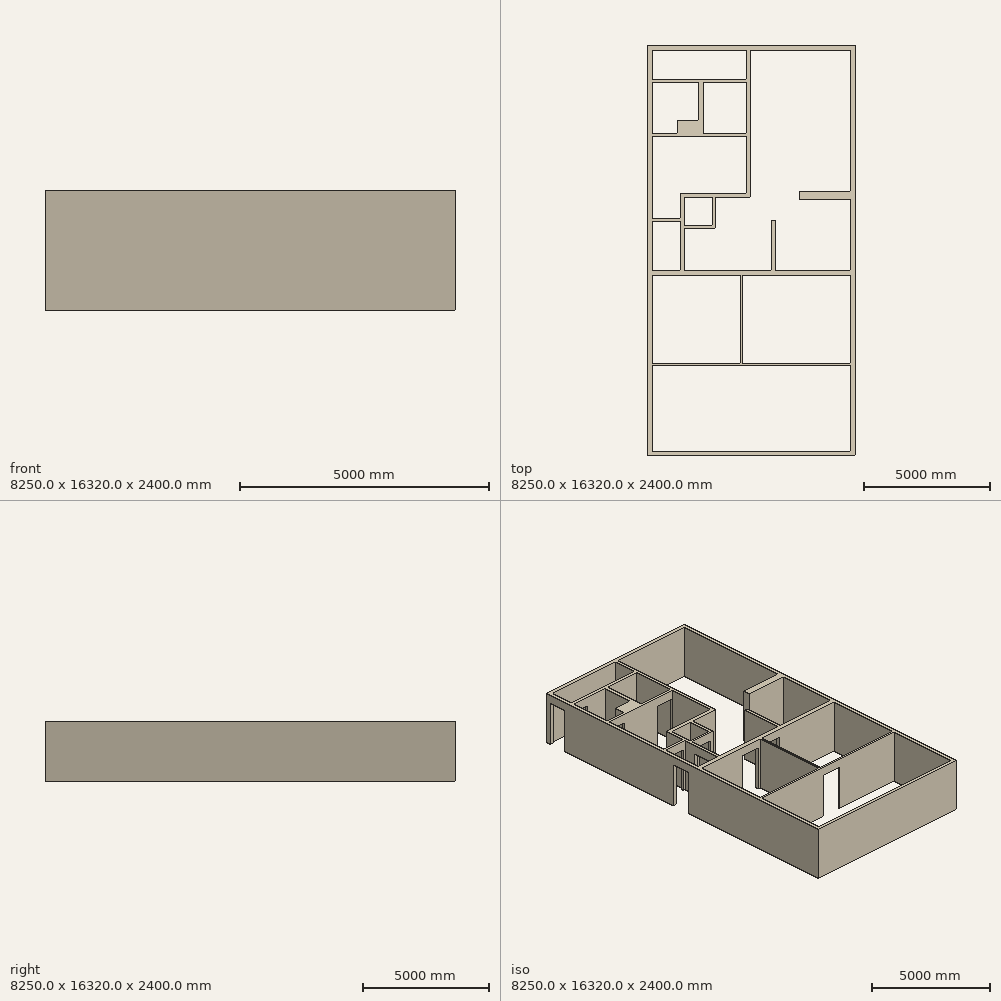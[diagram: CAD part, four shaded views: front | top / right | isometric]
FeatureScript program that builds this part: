
annotation { "Feature Type Name" : "Feature", "Feature Type Description" : "" }
export const myFeature = defineFeature(function(context is Context, id is Id, definition is map)
    precondition{}
    {
        {
            var Q0;
            Q0=qCreatedBy(makeId("Top.planeOp"),FACE);
            var sketch = newSketch(context, id + "F0", { "sketchPlane" : qUnion([Q0])});
            skLineSegment(sketch, "E0.bottom", {"start": v(-4125, 0) * mm, "end": v(4125, 0) * mm});
            skLineSegment(sketch, "E0.left", {"start": v(-4125, 0) * mm, "end": v(-4125, -9150) * mm});
            skLineSegment(sketch, "E0.right", {"start": v(4125, 0) * mm, "end": v(4125, -9150) * mm});
            skLineSegment(sketch, "E1.bottom", {"start": v(-3955, -200) * mm, "end": v(-195, -200) * mm});
            skLineSegment(sketch, "E1.top", {"start": v(-3955, -1340) * mm, "end": v(-195, -1340) * mm});
            skLineSegment(sketch, "E1.left", {"start": v(-3955, -200) * mm, "end": v(-3955, -1340) * mm});
            skLineSegment(sketch, "E1.right", {"start": v(-195, -200) * mm, "end": v(-195, -1340) * mm});
            skLineSegment(sketch, "E2.bottom", {"start": v(-3955, -1490) * mm, "end": v(-2105, -1490) * mm});
            skLineSegment(sketch, "E2.top", {"start": v(-3955, -3500) * mm, "end": v(-2105, -3500) * mm});
            skLineSegment(sketch, "E2.left", {"start": v(-3955, -1490) * mm, "end": v(-3955, -3500) * mm});
            skLineSegment(sketch, "E2.right", {"start": v(-2105, -1490) * mm, "end": v(-2105, -3500) * mm});
            skLineSegment(sketch, "E3.bottom", {"start": v(-1905, -1490) * mm, "end": v(-195, -1490) * mm});
            skLineSegment(sketch, "E3.top", {"start": v(-1905, -3500) * mm, "end": v(-195, -3500) * mm});
            skLineSegment(sketch, "E3.left", {"start": v(-1905, -1490) * mm, "end": v(-1905, -3500) * mm});
            skLineSegment(sketch, "E4.bottom", {"start": v(-3955, -3615) * mm, "end": v(-195, -3615) * mm});
            skLineSegment(sketch, "E4.top", {"start": v(-2825, -5885) * mm, "end": v(-195, -5885) * mm});
            skLineSegment(sketch, "E4.left", {"start": v(-3955, -3615) * mm, "end": v(-3955, -5885) * mm});
            skLineSegment(sketch, "E4.right", {"start": v(-195, -3615) * mm, "end": v(-195, -5885) * mm});
            skLineSegment(sketch, "E5.bottom", {"start": v(-2825, -6885) * mm, "end": v(-3955, -6885) * mm});
            skLineSegment(sketch, "E5.left", {"start": v(-2825, -6885) * mm, "end": v(-2825, -5885) * mm});
            skLineSegment(sketch, "E5.right", {"start": v(-3955, -6885) * mm, "end": v(-3955, -5885) * mm});
            skLineSegment(sketch, "E6.bottom", {"start": v(-3955, -8950) * mm, "end": v(-2825, -8950) * mm});
            skLineSegment(sketch, "E6.top", {"start": v(-3955, -7000) * mm, "end": v(-2825, -7000) * mm});
            skLineSegment(sketch, "E6.left", {"start": v(-3955, -8950) * mm, "end": v(-3955, -7000) * mm});
            skLineSegment(sketch, "E6.right", {"start": v(-2825, -8950) * mm, "end": v(-2825, -7000) * mm});
            skLineSegment(sketch, "E7.bottom", {"start": v(-2665, -6070) * mm, "end": v(-1545, -6070) * mm});
            skLineSegment(sketch, "E7.top", {"start": v(-2665, -7170) * mm, "end": v(-1545, -7170) * mm});
            skLineSegment(sketch, "E7.left", {"start": v(-2665, -6070) * mm, "end": v(-2665, -7170) * mm});
            skLineSegment(sketch, "E7.right", {"start": v(-1545, -6070) * mm, "end": v(-1545, -7170) * mm});
            skLineSegment(sketch, "E8.bottom", {"start": v(-45, -200) * mm, "end": v(3955, -200) * mm});
            skLineSegment(sketch, "E8.top", {"start": v(1905, -5800) * mm, "end": v(3955, -5800) * mm});
            skLineSegment(sketch, "E8.right", {"start": v(3955, -200) * mm, "end": v(3955, -5800) * mm});
            skLineSegment(sketch, "E9.bottom", {"start": v(3955, -8950) * mm, "end": v(955, -8950) * mm});
            skLineSegment(sketch, "E9.top", {"start": v(3955, -6120) * mm, "end": v(1905, -6120) * mm});
            skLineSegment(sketch, "E9.left", {"start": v(3955, -8950) * mm, "end": v(3955, -6120) * mm});
            skLineSegment(sketch, "E9.right", {"start": v(955, -8950) * mm, "end": v(955, -6950) * mm});
            skLineSegment(sketch, "E10.bottom", {"start": v(805, -8950) * mm, "end": v(-2665, -8950) * mm});
            skLineSegment(sketch, "E10.top", {"start": v(-1415, -7270) * mm, "end": v(-2665, -7270) * mm});
            skLineSegment(sketch, "E10.right", {"start": v(-2665, -8950) * mm, "end": v(-2665, -7270) * mm});
            skLineSegment(sketch, "E11.left", {"start": v(-1415, -6070) * mm, "end": v(-1415, -7270) * mm});
            skLineSegment(sketch, "E12", {"start": v(-2955, -3500) * mm, "end": v(-2955, -2970) * mm});
            skLineSegment(sketch, "E13", {"start": v(-2955, -2970) * mm, "end": v(-2105, -2970) * mm});
            skLineSegment(sketch, "E14", {"start": v(-195, -1490) * mm, "end": v(-195, -3500) * mm});
            skLineSegment(sketch, "E15", {"start": v(805, -8950) * mm, "end": v(805, -6950) * mm});
            skLineSegment(sketch, "E16", {"start": v(805, -6950) * mm, "end": v(955, -6950) * mm});
            skLineSegment(sketch, "E17", {"start": v(1905, -6120) * mm, "end": v(1905, -5800) * mm});
            skLineSegment(sketch, "E18", {"start": v(-1415, -6070) * mm, "end": v(-45, -6070) * mm});
            skLineSegment(sketch, "E19", {"start": v(-45, -6070) * mm, "end": v(-45, -200) * mm});
            skLineSegment(sketch, "E20", {"start": v(-4125, -9150) * mm, "end": v(4125, -9150) * mm});
            skLineSegment(sketch, "E21", {"start": v(-4125, -9150) * mm, "end": v(-4125, -16320) * mm});
            skLineSegment(sketch, "E22", {"start": v(-4125, -16320) * mm, "end": v(4125, -16320) * mm});
            skLineSegment(sketch, "E23", {"start": v(4125, -16320) * mm, "end": v(4125, -9150) * mm});
            skLineSegment(sketch, "E24", {"start": v(-3955, -9150) * mm, "end": v(-3955, -16150) * mm});
            skLineSegment(sketch, "E25", {"start": v(-3955, -16150) * mm, "end": v(3955, -16150) * mm});
            skLineSegment(sketch, "E26", {"start": v(3955, -16150) * mm, "end": v(3955, -9150) * mm});
            skLineSegment(sketch, "E27", {"start": v(-455, -9150) * mm, "end": v(-455, -12650) * mm});
            skLineSegment(sketch, "E28", {"start": v(-355, -12650) * mm, "end": v(-355, -9150) * mm});
            skLineSegment(sketch, "E29", {"start": v(-455, -12650) * mm, "end": v(-3955, -12650) * mm});
            skLineSegment(sketch, "E30", {"start": v(-3955, -12650) * mm, "end": v(-3955, -12750) * mm});
            skLineSegment(sketch, "E31", {"start": v(-355, -12750) * mm, "end": v(-3955, -12750) * mm});
            skLineSegment(sketch, "E32", {"start": v(-355, -12750) * mm, "end": v(3955, -12750) * mm});
            skLineSegment(sketch, "E33", {"start": v(-355, -12650) * mm, "end": v(3955, -12650) * mm});
            skSolve(sketch);
        }
        {
            var Q0;
            Q0=makeQuery(id+"F0.imprint","IMPRINT",FACE,{"disambiguationData":[TD([[makeQuery(id+"F0.imprint","IMPRINT",EDGE,{"derivedFrom":sQuery(id+"F0.wireOp",EDGE,"E0.bottom")}),-1.0]])]});
            var Q1;
            {var subQ3=sQuery(id+"F0.wireOp",EDGE,"E12");Q1=makeQuery(id+"F0.imprint","IMPRINT",FACE,{"disambiguationData":[TD([[makeQuery(id+"F0.imprint","IMPRINT",EDGE,{"derivedFrom":subQ3}),-1.0]])]});}
            var Q2;
            {var subQ0=sQuery(id+"F0.wireOp",EDGE,"E27");Q2=makeQuery(id+"F0.imprint","IMPRINT",FACE,{"disambiguationData":[TD([[makeQuery(id+"F0.imprint","IMPRINT",EDGE,{"derivedFrom":subQ0}),1.0]])]});}
            var Q3;
            {var subQ10=sQuery(id+"F0.wireOp",EDGE,"E21");Q3=makeQuery(id+"F0.imprint","IMPRINT",FACE,{"disambiguationData":[TD([[makeQuery(id+"F0.imprint","IMPRINT",EDGE,{"derivedFrom":subQ10}),1.0]])]});}
            extrude(context, id + "F1", {"entities" : qUnion([Q0, Q1, Q2, Q3]), "depth" : 2400 * mm});
        }
        {
            var Q0;
            Q0=makeQuery(id+"F1.opExtrude","CAP_FACE",FACE,{"disambiguationData":[OSD([sQuery(id+"F0.wireOp",EDGE,"E0.bottom"),sQuery(id+"F0.wireOp",EDGE,"E0.left"),sQuery(id+"F0.wireOp",EDGE,"E0.right"),sQuery(id+"F0.wireOp",EDGE,"E1.bottom"),sQuery(id+"F0.wireOp",EDGE,"E1.top"),sQuery(id+"F0.wireOp",EDGE,"E1.left"),sQuery(id+"F0.wireOp",EDGE,"E1.right"),sQuery(id+"F0.wireOp",EDGE,"E2.bottom"),sQuery(id+"F0.wireOp",EDGE,"E2.top"),sQuery(id+"F0.wireOp",EDGE,"E2.left"),sQuery(id+"F0.wireOp",EDGE,"E2.right"),sQuery(id+"F0.wireOp",EDGE,"E3.bottom"),sQuery(id+"F0.wireOp",EDGE,"E3.top"),sQuery(id+"F0.wireOp",EDGE,"E3.left"),sQuery(id+"F0.wireOp",EDGE,"E4.bottom"),sQuery(id+"F0.wireOp",EDGE,"E4.top"),sQuery(id+"F0.wireOp",EDGE,"E4.left"),sQuery(id+"F0.wireOp",EDGE,"E4.right"),sQuery(id+"F0.wireOp",EDGE,"E5.bottom"),sQuery(id+"F0.wireOp",EDGE,"E5.left"),sQuery(id+"F0.wireOp",EDGE,"E5.right"),sQuery(id+"F0.wireOp",EDGE,"E6.bottom"),sQuery(id+"F0.wireOp",EDGE,"E6.top"),sQuery(id+"F0.wireOp",EDGE,"E6.left"),sQuery(id+"F0.wireOp",EDGE,"E6.right"),sQuery(id+"F0.wireOp",EDGE,"E7.bottom"),sQuery(id+"F0.wireOp",EDGE,"E7.top"),sQuery(id+"F0.wireOp",EDGE,"E7.left"),sQuery(id+"F0.wireOp",EDGE,"E7.right"),sQuery(id+"F0.wireOp",EDGE,"E8.bottom"),sQuery(id+"F0.wireOp",EDGE,"E8.top"),sQuery(id+"F0.wireOp",EDGE,"E8.right"),sQuery(id+"F0.wireOp",EDGE,"E9.bottom"),sQuery(id+"F0.wireOp",EDGE,"E9.top"),sQuery(id+"F0.wireOp",EDGE,"E9.left"),sQuery(id+"F0.wireOp",EDGE,"E9.right"),sQuery(id+"F0.wireOp",EDGE,"E10.bottom"),sQuery(id+"F0.wireOp",EDGE,"E10.top"),sQuery(id+"F0.wireOp",EDGE,"E10.right"),sQuery(id+"F0.wireOp",EDGE,"E11.left"),sQuery(id+"F0.wireOp",EDGE,"E12"),sQuery(id+"F0.wireOp",EDGE,"E13"),sQuery(id+"F0.wireOp",EDGE,"E14"),sQuery(id+"F0.wireOp",EDGE,"E15"),sQuery(id+"F0.wireOp",EDGE,"E16"),sQuery(id+"F0.wireOp",EDGE,"E17"),sQuery(id+"F0.wireOp",EDGE,"E18"),sQuery(id+"F0.wireOp",EDGE,"E19"),sQuery(id+"F0.wireOp",EDGE,"E20"),sQuery(id+"F0.wireOp",EDGE,"E21"),sQuery(id+"F0.wireOp",EDGE,"E22"),sQuery(id+"F0.wireOp",EDGE,"E23"),sQuery(id+"F0.wireOp",EDGE,"E24"),sQuery(id+"F0.wireOp",EDGE,"E25"),sQuery(id+"F0.wireOp",EDGE,"E26"),sQuery(id+"F0.wireOp",EDGE,"E27"),sQuery(id+"F0.wireOp",EDGE,"E28"),sQuery(id+"F0.wireOp",EDGE,"E29"),sQuery(id+"F0.wireOp",EDGE,"E31"),sQuery(id+"F0.wireOp",EDGE,"E32"),sQuery(id+"F0.wireOp",EDGE,"E33")])],"isStart":false});
            var sketch = newSketch(context, id + "F2", { "sketchPlane" : qUnion([Q0])});
            skLineSegment(sketch, "E34", {"start": v(-2665, -7570) * mm, "end": v(-2825, -7570) * mm});
            skLineSegment(sketch, "E35", {"start": v(-2825, -7570) * mm, "end": v(-2825, -8450) * mm});
            skLineSegment(sketch, "E36", {"start": v(-2825, -8450) * mm, "end": v(-2665, -8450) * mm});
            skLineSegment(sketch, "E37", {"start": v(-2215, -7170) * mm, "end": v(-2215, -7270) * mm});
            skLineSegment(sketch, "E38", {"start": v(-2215, -7270) * mm, "end": v(-1565, -7270) * mm});
            skLineSegment(sketch, "E39", {"start": v(-1565, -7270) * mm, "end": v(-1565, -7170) * mm});
            skLineSegment(sketch, "E40", {"start": v(-3755, -6885) * mm, "end": v(-3755, -7000) * mm});
            skLineSegment(sketch, "E41", {"start": v(-3755, -7000) * mm, "end": v(-2905, -7000) * mm});
            skLineSegment(sketch, "E42", {"start": v(-2905, -7000) * mm, "end": v(-2905, -6885) * mm});
            skLineSegment(sketch, "E43", {"start": v(-205, -3500) * mm, "end": v(-205, -3615) * mm});
            skLineSegment(sketch, "E44", {"start": v(-205, -3615) * mm, "end": v(-1075, -3615) * mm});
            skLineSegment(sketch, "E45", {"start": v(-1075, -3615) * mm, "end": v(-1075, -3500) * mm});
            skLineSegment(sketch, "E46", {"start": v(-3935, -3500) * mm, "end": v(-3935, -3615) * mm});
            skLineSegment(sketch, "E47", {"start": v(-3935, -3615) * mm, "end": v(-3055, -3615) * mm});
            skLineSegment(sketch, "E48", {"start": v(-3055, -3615) * mm, "end": v(-3055, -1490) * mm});
            skLineSegment(sketch, "E49", {"start": v(-3935, -1340) * mm, "end": v(-3935, -1490) * mm});
            skLineSegment(sketch, "E50", {"start": v(-3935, -1490) * mm, "end": v(-3135, -1490) * mm});
            skLineSegment(sketch, "E51", {"start": v(-3135, -1490) * mm, "end": v(-3135, -1340) * mm});
            skLineSegment(sketch, "E52", {"start": v(-4125, -7620) * mm, "end": v(-3955, -7620) * mm});
            skLineSegment(sketch, "E53", {"start": v(-3955, -7620) * mm, "end": v(-3955, -8500) * mm});
            skLineSegment(sketch, "E54", {"start": v(-3955, -8500) * mm, "end": v(-4125, -8500) * mm});
            skLineSegment(sketch, "E55", {"start": v(-3955, -240) * mm, "end": v(-4125, -240) * mm});
            skLineSegment(sketch, "E56", {"start": v(-4125, -240) * mm, "end": v(-4125, -1090) * mm});
            skLineSegment(sketch, "E57", {"start": v(-4125, -1090) * mm, "end": v(-3955, -1090) * mm});
            skLineSegment(sketch, "E58", {"start": v(-1505, -9150) * mm, "end": v(-1505, -8950) * mm});
            skLineSegment(sketch, "E59", {"start": v(-1505, -8950) * mm, "end": v(-555, -8950) * mm});
            skLineSegment(sketch, "E60", {"start": v(-555, -8950) * mm, "end": v(-555, -9150) * mm});
            skLineSegment(sketch, "E61", {"start": v(-255, -9150) * mm, "end": v(-255, -8950) * mm});
            skLineSegment(sketch, "E62", {"start": v(-255, -8950) * mm, "end": v(695, -8950) * mm});
            skLineSegment(sketch, "E63", {"start": v(695, -8950) * mm, "end": v(695, -9150) * mm});
            skLineSegment(sketch, "E64", {"start": v(-255, -12650) * mm, "end": v(-255, -12750) * mm});
            skLineSegment(sketch, "E65", {"start": v(-255, -12750) * mm, "end": v(695, -12750) * mm});
            skLineSegment(sketch, "E66", {"start": v(695, -12750) * mm, "end": v(695, -12650) * mm});
            skSolve(sketch);
        }
        {
            var Q0;
            {var subQ0=sQuery(id+"F2.wireOp",EDGE,"E55");Q0=makeQuery(id+"F2.imprint","IMPRINT",FACE,{"disambiguationData":[TD([[makeQuery(id+"F2.imprint","IMPRINT",EDGE,{"derivedFrom":subQ0}),1.0]])]});}
            var Q1;
            {var subQ0=sQuery(id+"F2.wireOp",EDGE,"E49");Q1=makeQuery(id+"F2.imprint","IMPRINT",FACE,{"disambiguationData":[TD([[makeQuery(id+"F2.imprint","IMPRINT",EDGE,{"derivedFrom":subQ0}),1.0]])]});}
            var Q2;
            {var subQ0=sQuery(id+"F2.wireOp",EDGE,"E46");Q2=makeQuery(id+"F2.imprint","IMPRINT",FACE,{"disambiguationData":[TD([[makeQuery(id+"F2.imprint","IMPRINT",EDGE,{"derivedFrom":subQ0}),1.0]])]});}
            var Q3;
            {var subQ0=sQuery(id+"F2.wireOp",EDGE,"E43");Q3=makeQuery(id+"F2.imprint","IMPRINT",FACE,{"disambiguationData":[TD([[makeQuery(id+"F2.imprint","IMPRINT",EDGE,{"derivedFrom":subQ0}),-1.0]])]});}
            var Q4;
            {var subQ0=sQuery(id+"F2.wireOp",EDGE,"E40");Q4=makeQuery(id+"F2.imprint","IMPRINT",FACE,{"disambiguationData":[TD([[makeQuery(id+"F2.imprint","IMPRINT",EDGE,{"derivedFrom":subQ0}),1.0]])]});}
            var Q5;
            {var subQ0=sQuery(id+"F2.wireOp",EDGE,"E52");Q5=makeQuery(id+"F2.imprint","IMPRINT",FACE,{"disambiguationData":[TD([[makeQuery(id+"F2.imprint","IMPRINT",EDGE,{"derivedFrom":subQ0}),-1.0]])]});}
            var Q6;
            {var subQ0=sQuery(id+"F2.wireOp",EDGE,"E37");Q6=makeQuery(id+"F2.imprint","IMPRINT",FACE,{"disambiguationData":[TD([[makeQuery(id+"F2.imprint","IMPRINT",EDGE,{"derivedFrom":subQ0}),1.0]])]});}
            var Q7;
            {var subQ0=sQuery(id+"F2.wireOp",EDGE,"E34");Q7=makeQuery(id+"F2.imprint","IMPRINT",FACE,{"disambiguationData":[TD([[makeQuery(id+"F2.imprint","IMPRINT",EDGE,{"derivedFrom":subQ0}),1.0]])]});}
            var Q8;
            {var subQ0=sQuery(id+"F2.wireOp",EDGE,"bXyyP22b-Fd5s-pKkp-Mfep-lPmGgl1eoEIG");Q8=makeQuery(id+"F2.imprint","IMPRINT",FACE,{"disambiguationData":[TD([[makeQuery(id+"F2.imprint","IMPRINT",EDGE,{"derivedFrom":subQ0}),-1.0]])]});}
            var Q9;
            {var subQ0=sQuery(id+"F2.wireOp",EDGE,"KmRBw4Ro-Tt1S-G3wa-DgO3-rAmxpNFbD2dc");Q9=makeQuery(id+"F2.imprint","IMPRINT",FACE,{"disambiguationData":[TD([[makeQuery(id+"F2.imprint","IMPRINT",EDGE,{"derivedFrom":subQ0}),1.0]])]});}
            var Q10;
            {var subQ0=sQuery(id+"F2.wireOp",EDGE,"DsypGBD1-VUyX-LvVu-Ju5p-gGMJGe04lbca");Q10=makeQuery(id+"F2.imprint","IMPRINT",FACE,{"disambiguationData":[TD([[makeQuery(id+"F2.imprint","IMPRINT",EDGE,{"derivedFrom":subQ0}),1.0]])]});}
            var Q11;
            {var subQ0=sQuery(id+"F2.wireOp",EDGE,"xUU9sHKB-wWJu-vvyQ-Y27K-SafOuSSaSPCu");Q11=makeQuery(id+"F2.imprint","IMPRINT",FACE,{"disambiguationData":[TD([[makeQuery(id+"F2.imprint","IMPRINT",EDGE,{"derivedFrom":subQ0}),1.0]])]});}
            var Q12;
            {var subQ0=sQuery(id+"F2.wireOp",EDGE,"gtOgTZcF-iGIu-P8De-4s3f-iU6d5bzWKqcu");Q12=makeQuery(id+"F2.imprint","IMPRINT",FACE,{"disambiguationData":[TD([[makeQuery(id+"F2.imprint","IMPRINT",EDGE,{"derivedFrom":subQ0}),-1.0]])]});}
            var Q13;
            {var subQ0=sQuery(id+"F2.wireOp",EDGE,"w5LqMJMD-BTsf-lrcy-2qe3-qbSku6zuDei2");Q13=makeQuery(id+"F2.imprint","IMPRINT",FACE,{"disambiguationData":[TD([[makeQuery(id+"F2.imprint","IMPRINT",EDGE,{"derivedFrom":subQ0}),1.0]])]});}
            var Q14;
            {var subQ0=sQuery(id+"F2.wireOp",EDGE,"gPe3p3GD-z5Sc-NsmL-BG3g-iFZIMeydH4XN");Q14=makeQuery(id+"F2.imprint","IMPRINT",FACE,{"disambiguationData":[TD([[makeQuery(id+"F2.imprint","IMPRINT",EDGE,{"derivedFrom":subQ0}),1.0]])]});}
            var Q15;
            {var subQ0=sQuery(id+"F2.wireOp",EDGE,"yB4fgNzf-4WXd-bTIO-ROpB-tO7Q6PLyojeI");Q15=makeQuery(id+"F2.imprint","IMPRINT",FACE,{"disambiguationData":[TD([[makeQuery(id+"F2.imprint","IMPRINT",EDGE,{"derivedFrom":subQ0}),-1.0]])]});}
            var Q16;
            {var subQ0=sQuery(id+"F2.wireOp",EDGE,"iTkjHG0i-oWPG-WNHC-gP18-lA7tzI3W6FOF");Q16=makeQuery(id+"F2.imprint","IMPRINT",FACE,{"disambiguationData":[TD([[makeQuery(id+"F2.imprint","IMPRINT",EDGE,{"derivedFrom":subQ0}),-1.0]])]});}
            var Q17;
            {var subQ0=sQuery(id+"F2.wireOp",EDGE,"AnUvtcCU-d7Ku-vRum-K7dT-Ix1SRXOT5qH1");Q17=makeQuery(id+"F2.imprint","IMPRINT",FACE,{"disambiguationData":[TD([[makeQuery(id+"F2.imprint","IMPRINT",EDGE,{"derivedFrom":subQ0}),-1.0]])]});}
            var Q18;
            {var subQ0=sQuery(id+"F2.wireOp",EDGE,"E58");Q18=makeQuery(id+"F2.imprint","IMPRINT",FACE,{"disambiguationData":[TD([[makeQuery(id+"F2.imprint","IMPRINT",EDGE,{"derivedFrom":subQ0}),-1.0]])]});}
            var Q19;
            {var subQ0=sQuery(id+"F2.wireOp",EDGE,"E61");Q19=makeQuery(id+"F2.imprint","IMPRINT",FACE,{"disambiguationData":[TD([[makeQuery(id+"F2.imprint","IMPRINT",EDGE,{"derivedFrom":subQ0}),-1.0]])]});}
            var Q20;
            {var subQ0=sQuery(id+"F2.wireOp",EDGE,"E64");Q20=makeQuery(id+"F2.imprint","IMPRINT",FACE,{"disambiguationData":[TD([[makeQuery(id+"F2.imprint","IMPRINT",EDGE,{"derivedFrom":subQ0}),1.0]])]});}
            extrude(context, id + "F3", {"entities" : qUnion([Q0, Q1, Q2, Q3, Q4, Q5, Q6, Q7, Q8, Q9, Q10, Q11, Q12, Q13, Q14, Q15, Q16, Q17, Q18, Q19, Q20]), "operationType" : NewBodyOperationType.REMOVE, "endBound" : BoundingType.UP_TO_NEXT, "oppositeDirection" : true, "depth" : 2200 * mm, "hasSecondDirection" : true, "secondDirectionOppositeDirection" : true, "secondDirectionDepth" : 400 * mm});
        }
    });
